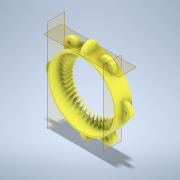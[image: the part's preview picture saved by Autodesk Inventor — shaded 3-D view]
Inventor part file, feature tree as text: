
AUTODESK INVENTOR PART (.ipt)
format: ipt  version: 2021.2 (Build 252289000, 289)  size: 795,136 bytes
history: native  units: in
note: dims shown in document units (in); Inventor stores cm internally (conversion verified against a paired STEP export)
features: extrude x8, sketch x8, plane x3, pattern_circular x3, fillet x2
ambient origin geometry x8: Origin, YZ Plane, XZ Plane, XY Plane, X Axis, Y Axis, Z Axis, Center Point
bodies: Solid1 (feature_tree)
feature tree (24):
  extrude  "Extrusion1"  Depth=4.25in
  plane  "Work Plane1"
  plane  "Work Plane2"
  extrude  "Extrusion3"  Depth=1.4in
  fillet  "Fillet1"  Radius=2.125in
  extrude  "Extrusion4"  TaperAngle=0.0deg  [1 undecoded]
  pattern_circular  "Circular Pattern2"  Count=2 Angle=360.0deg
  plane  "Work Plane3"
  extrude  "Extrusion5"  [1 undecoded]
  extrude  "Extrusion6"  Depth=1.0in
  fillet  "Fillet2"  Radius=0.25in
  extrude  "Extrusion7"  Depth=0.5in
  pattern_circular  "Circular Pattern3"  [2 undecoded]
  extrude  "Extrusion14"  Depth=0.1in TaperAngle=0.0deg
  pattern_circular  "Circular Pattern9"  [2 undecoded]
  extrude  "Extrusion15"  Depth=0.5in
  sketch  "Sketch1"  dims[d0=4.0in d1=4.25in]
  sketch  "Sketch3"  dims[d2=1.0in d3=0.0in d4=1.4in d10=2.125in]
  sketch  "Sketch4"  dims[d11=0.25in d12=0.0in]
  sketch  "Sketch5"  dims[d13=0.5in d14=0.0in]
  sketch  "Sketch6"  dims[d15=0.5in]
  sketch  "Sketch7"  dims[d16=0.125in]
  sketch  "Sketch8"  dims[d17=0.2in]
  sketch  "Sketch11"  dims[d18=0.5in d19=0.0in d20=0.7874in d21=360.0deg d23=-2.125in d24=1.0in d25=0.25in d26=0.5in d27=0.0in d28=0.1in d29=0.0in d30=0.5in d31=0.0in d32=0.5in d33=0.25in d34=0.2in d35=0.5in d36=0.0in d37=2.3622in d38=360.0deg d40=0.25in d41=0.125in d42=0.25in d43=0.2in d49=0.5in d50=0.0312in d79=0.65in d80=0.0in d81=18.8976in d82=360.0deg d84=3.0625in d85=0.0in d86=0.0777in]
note: 6 required parameter values undecoded (feature->parameter linkage not recoverable at this tier; creation-order binding heuristic only, values carry confidence <= 0.55)
